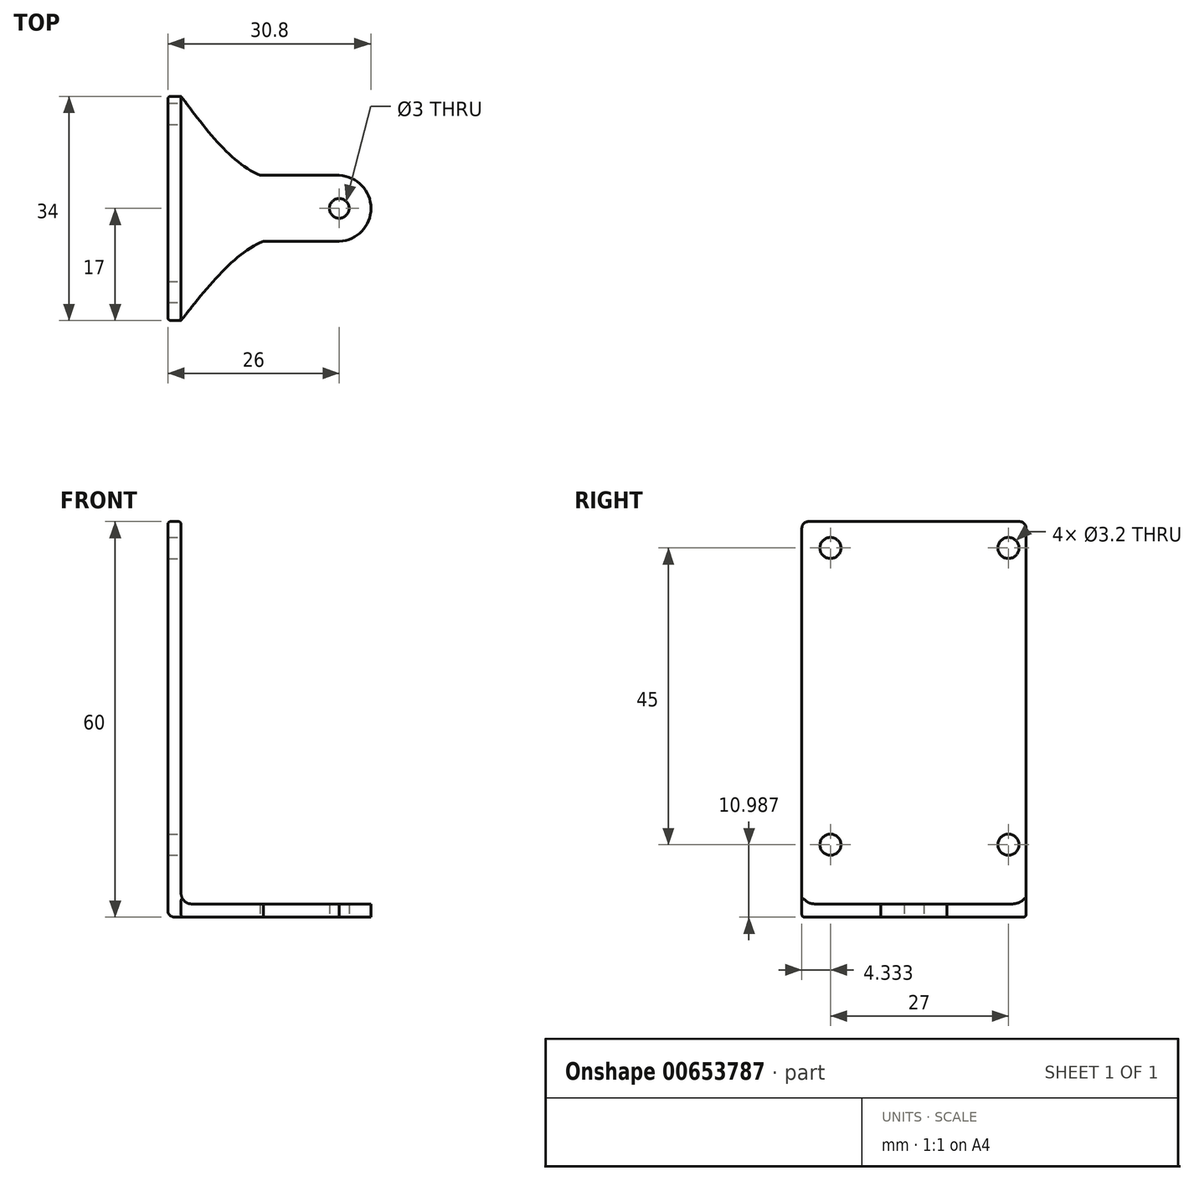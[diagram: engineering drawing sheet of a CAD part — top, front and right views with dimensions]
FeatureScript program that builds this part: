
annotation { "Feature Type Name" : "Feature", "Feature Type Description" : "" }
export const myFeature = defineFeature(function(context is Context, id is Id, definition is map)
    precondition{}
    {
        {
            var Q0;
            Q0=qCreatedBy(makeId("Top.planeOp"),FACE);
            var sketch = newSketch(context, id + "F0", { "sketchPlane" : qUnion([Q0])});
            skLineSegment(sketch, "E0.bottom", {"start": v(13.5, -5) * mm, "end": v(25, -5) * mm});
            skLineSegment(sketch, "E0.top", {"start": v(13, 5) * mm, "end": v(25, 5) * mm});
            skCircle(sketch, "E1", {"center": v(25, 0) * mm, "radius": 1.5 * mm});
            skArc(sketch, "E2", {"start": v(25, -5) * mm, "mid": v(29.8, 0) * mm, "end": v(25, 5) * mm});
            skPoint(sketch, "E2.third.point", {"position": v(29.62, 1.35) * mm});
            skLineSegment(sketch, "E3.bottom", {"start": v(-1, 17) * mm, "end": v(1, 17) * mm});
            skLineSegment(sketch, "E3.top", {"start": v(-1, -17) * mm, "end": v(1, -17) * mm});
            skLineSegment(sketch, "E3.left", {"start": v(-1, 17) * mm, "end": v(-1, -17) * mm});
            skLineSegment(sketch, "E3.right", {"start": v(1, 17) * mm, "end": v(1, -17) * mm});
            skPoint(sketch, "E3.middle", {"position": v(0, 0) * mm});
            skFitSpline(sketch, "E4", {"points": [v(1, 17) * mm, v(1, 5) * mm], "startDerivative": vector(0, -12) * mm, "endDerivative": vector(0, -12) * mm});
            skFitSpline(sketch, "E5", {"points": [v(1, 17) * mm, v(13, 5) * mm, v(25, 5) * mm], "startDerivative": vector(20.96, -28.1) * mm, "endDerivative": vector(27.23, 5.05) * mm});
            skFitSpline(sketch, "E6", {"points": [v(1, -17) * mm, v(13.5, -5) * mm, v(25, -5) * mm], "startDerivative": vector(21.88, 27.77) * mm, "endDerivative": vector(26.27, -4.89) * mm});
            skSolve(sketch);
        }
        {
            var Q0;
            Q0 = qSketchRegion(id + "F0", true);
            extrude(context, id + "F1", {"entities" : qUnion([Q0]), "depth" : 2 * mm, "offsetDistance" : 25 * mm});
        }
        {
            var Q0;
            Q0=makeQuery(id+"F0.imprint","IMPRINT",FACE,{"disambiguationData":[TD([[makeQuery(id+"F0.imprint","IMPRINT",EDGE,{"derivedFrom":sQuery(id+"F0.wireOp",EDGE,"E3.bottom")}),-1.0]])]});
            extrude(context, id + "F2", {"entities" : qUnion([Q0]), "operationType" : NewBodyOperationType.ADD, "depth" : 60 * mm, "offsetDistance" : 25 * mm});
        }
        {
            var Q0;
            Q0=makeQuery(id+"F2.opExtrude","SWEPT_FACE",FACE,{"disambiguationData":[OSD([sQuery(id+"F0.wireOp",EDGE,"E3.right")])]});
            var sketch = newSketch(context, id + "F3", { "sketchPlane" : qUnion([Q0])});
            skCircle(sketch, "E7", {"center": v(-12.67, 55.99) * mm, "radius": 1.6 * mm});
            skCircle(sketch, "E8", {"center": v(14.33, 55.99) * mm, "radius": 1.6 * mm});
            skCircle(sketch, "E9", {"center": v(14.33, 10.99) * mm, "radius": 1.6 * mm});
            skCircle(sketch, "E10", {"center": v(-12.67, 10.99) * mm, "radius": 1.6 * mm});
            skSolve(sketch);
        }
        {
            var Q0;
            Q0=makeQuery(id+"F3.imprint","IMPRINT",FACE,{"disambiguationData":[TD([[makeQuery(id+"F3.imprint","IMPRINT",EDGE,{"derivedFrom":sQuery(id+"F3.wireOp",EDGE,"E7")}),1.0]])]});
            var Q1;
            Q1=makeQuery(id+"F3.imprint","IMPRINT",FACE,{"disambiguationData":[TD([[makeQuery(id+"F3.imprint","IMPRINT",EDGE,{"derivedFrom":sQuery(id+"F3.wireOp",EDGE,"E8")}),1.0]])]});
            var Q2;
            Q2=makeQuery(id+"F3.imprint","IMPRINT",FACE,{"disambiguationData":[TD([[makeQuery(id+"F3.imprint","IMPRINT",EDGE,{"derivedFrom":sQuery(id+"F3.wireOp",EDGE,"E9")}),1.0]])]});
            var Q3;
            Q3=makeQuery(id+"F3.imprint","IMPRINT",FACE,{"disambiguationData":[TD([[makeQuery(id+"F3.imprint","IMPRINT",EDGE,{"derivedFrom":sQuery(id+"F3.wireOp",EDGE,"E10")}),1.0]])]});
            extrude(context, id + "F4", {"entities" : qUnion([Q0, Q1, Q2, Q3]), "operationType" : NewBodyOperationType.REMOVE, "oppositeDirection" : true, "depth" : 3 * mm, "offsetDistance" : 25 * mm});
        }
        {
            var Q0;
            Q0=makeQuery(id+"F2.boolean.opBoolean","INTERSECT",EDGE,{"derivedFrom":[makeQuery(id+"F1.opExtrude","CAP_FACE",FACE,{"disambiguationData":[OSD([sQuery(id+"F0.wireOp",EDGE,"E0.bottom"),sQuery(id+"F0.wireOp",EDGE,"E0.top"),sQuery(id+"F0.wireOp",EDGE,"E1"),sQuery(id+"F0.wireOp",EDGE,"E2"),sQuery(id+"F0.wireOp",EDGE,"E3.bottom"),sQuery(id+"F0.wireOp",EDGE,"E3.top"),sQuery(id+"F0.wireOp",EDGE,"E3.left"),sQuery(id+"F0.wireOp",EDGE,"E5"),sQuery(id+"F0.wireOp",EDGE,"E6")])],"isStart":false}),makeQuery(id+"F2.opExtrude","SWEPT_FACE",FACE,{"disambiguationData":[OSD([sQuery(id+"F0.wireOp",EDGE,"E3.right")])]})]});
            fillet(context, id + "F5", {"entities" : qUnion([Q0]), "radius" : 1.6 * mm, "tangentPropagation" : true, "allowEdgeOverflow" : false});
        }
        {
            var Q0;
            Q0=makeQuery(id+"F2.opExtrude","CAP_EDGE",EDGE,{"disambiguationData":[OSD([sQuery(id+"F0.wireOp",EDGE,"E3.top")])],"isStart":false});
            fillet(context, id + "F6", {"entities" : qUnion([Q0]), "radius" : 1 * mm, "tangentPropagation" : true, "allowEdgeOverflow" : false});
        }
        {
            var Q0;
            Q0=makeQuery(id+"F2.opExtrude","CAP_EDGE",EDGE,{"disambiguationData":[OSD([sQuery(id+"F0.wireOp",EDGE,"E3.bottom")])],"isStart":false});
            fillet(context, id + "F7", {"entities" : qUnion([Q0]), "radius" : 1 * mm, "tangentPropagation" : true, "allowEdgeOverflow" : false});
        }
        {
            var Q0;
            Q0=makeQuery(id+"F1.opExtrude","CAP_EDGE",EDGE,{"disambiguationData":[OSD([sQuery(id+"F0.wireOp",EDGE,"E3.left")])],"isStart":true});
            fillet(context, id + "F8", {"entities" : qUnion([Q0]), "radius" : 1 * mm, "tangentPropagation" : true, "allowEdgeOverflow" : false});
        }
        {
            var Q0;
            Q0=makeQuery(id+"F2.opExtrude","SWEPT_EDGE",EDGE,{"disambiguationData":[OSD([sQuery(id+"F0.wireOp",EDGE,"E3.bottom"),sQuery(id+"F0.wireOp",EDGE,"E5"),sQuery(id+"F0.wireOp",EDGE,"E3.right")])]});
            var Q1;
            {var subQ0=sQuery(id+"F0.wireOp",EDGE,"E3.left");var subQ1=sQuery(id+"F0.wireOp",EDGE,"E3.bottom");Q1=makeQuery(id+"F2.boolean.opBoolean","MERGE",EDGE,{"derivedFrom":[makeQuery(id+"F1.opExtrude","SWEPT_EDGE",EDGE,{"disambiguationData":[OSD([subQ1,subQ0])]}),makeQuery(id+"F2.opExtrude","SWEPT_EDGE",EDGE,{"disambiguationData":[OSD([subQ1,subQ0])]})]});}
            var Q2;
            {var subQ0=sQuery(id+"F0.wireOp",EDGE,"E3.left");var subQ1=sQuery(id+"F0.wireOp",EDGE,"E3.top");Q2=makeQuery(id+"F2.boolean.opBoolean","MERGE",EDGE,{"derivedFrom":[makeQuery(id+"F1.opExtrude","SWEPT_EDGE",EDGE,{"disambiguationData":[OSD([subQ1,subQ0])]}),makeQuery(id+"F2.opExtrude","SWEPT_EDGE",EDGE,{"disambiguationData":[OSD([subQ1,subQ0])]})]});}
            var Q3;
            Q3=makeQuery(id+"F2.opExtrude","SWEPT_EDGE",EDGE,{"disambiguationData":[OSD([sQuery(id+"F0.wireOp",EDGE,"E3.top"),sQuery(id+"F0.wireOp",EDGE,"E6"),sQuery(id+"F0.wireOp",EDGE,"E3.right")])]});
            fillet(context, id + "F9", {"entities" : qUnion([Q0, Q1, Q2, Q3]), "radius" : 0.4 * mm, "tangentPropagation" : true, "allowEdgeOverflow" : false});
        }
    });
